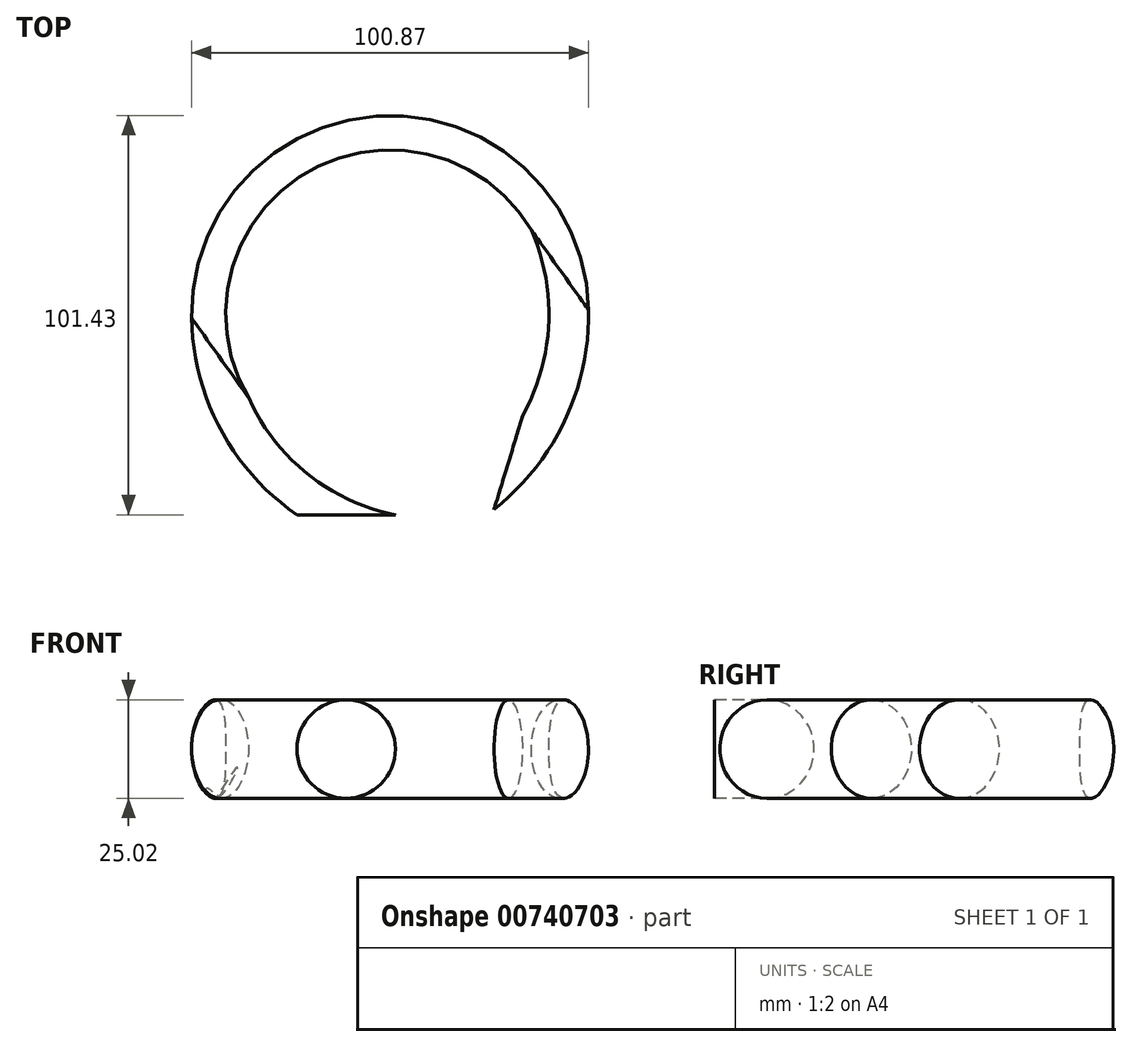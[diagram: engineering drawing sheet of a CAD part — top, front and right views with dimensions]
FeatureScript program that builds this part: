
annotation { "Feature Type Name" : "Feature", "Feature Type Description" : "" }
export const myFeature = defineFeature(function(context is Context, id is Id, definition is map)
    precondition{}
    {
        {
            var Q0;
            Q0=qCreatedBy(makeId("Top.planeOp"),FACE);
            var sketch = newSketch(context, id + "F0", { "sketchPlane" : qUnion([Q0])});
            skArc(sketch, "E0", {"start": v(47, 51) * mm, "mid": v(2.72, 95.28) * mm, "end": v(-41.57, 51) * mm});
            skArc(sketch, "E1", {"start": v(-41.57, 51) * mm, "mid": v(-35.39, 25.47) * mm, "end": v(-18.22, 5.6) * mm});
            skArc(sketch, "E2", {"start": v(47, 51) * mm, "mid": v(41.09, 25.68) * mm, "end": v(24.56, 5.6) * mm});
            skSolve(sketch);
        }
        {
            var Q0;
            Q0=qCreatedBy(makeId("Front.planeOp"),FACE);
            var sketch = newSketch(context, id + "F1", { "sketchPlane" : qUnion([Q0])});
            skCircle(sketch, "E3", {"center": v(-8.45, 0) * mm, "radius": 12.5 * mm});
            skSolve(sketch);
        }
        {
            var Q0;
            Q0=makeQuery(id+"F1.imprint","IMPRINT",FACE,{"disambiguationData":[TD([[makeQuery(id+"F1.imprint","IMPRINT",EDGE,{"derivedFrom":sQuery(id+"F1.wireOp",EDGE,"E3")}),1.0]])]});
            var Q1;
            Q1 = qConstructionFilter(qBodyType(qCreatedBy(id + "F0" ,EDGE), BodyType.WIRE), ConstructionObject.NO);
            sweep(context, id + "F2", {"profiles" : qUnion([Q0]), "path" : qUnion([Q1])});
        }
    });
